# Revit family: Fence_-_Wood_-_Vertical_Pickets_14964
name_source: partatom
category: Generic Models
revit_build: Autodesk Revit 2014 (Build: 20130308_1515(x64)
units: mm (PartAtom-declared; Revit-internal decimal feet)

## types (1)
- 6' High x 8' Span (Typ)
    Assembly Code = G2040100
    Depth Below Grade = 1' - 0"
    Fencing Material = Pine, Radiata
    Height = 6' - 0"
    Height Overall = 7' - 0"
    Model History = BIMforLAs, 2014.02.20
    Panel Depth = 0' - 0 1/4"
    Picket Base Offset = 0' - 3"
    Picket Depth = 0' - 0 3/4"
    Picket Height = 5' - 9"
    Picket Width = 0' - 5 1/2"
    Picket_Clear = 0' - 0 1/2"
    Picket_Dog Ear = Yes
    Picket_OC = 0' - 6"
    Picket_Square = No
    Post Depth = 0' - 3 1/2"
    Post Width = 0' - 3 1/2"
    Rail Depth = 0' - 1 1/2"
    Rail Width = 0' - 3 1/2"
    Rail1 Offset = 0' - 6"
    Rail2 Offset = 0' - 6"
    Show Rail 3 = No

## geometry (parser evidence)
native form markers: Sweep x8
no freeform markers — native parametric forms only
